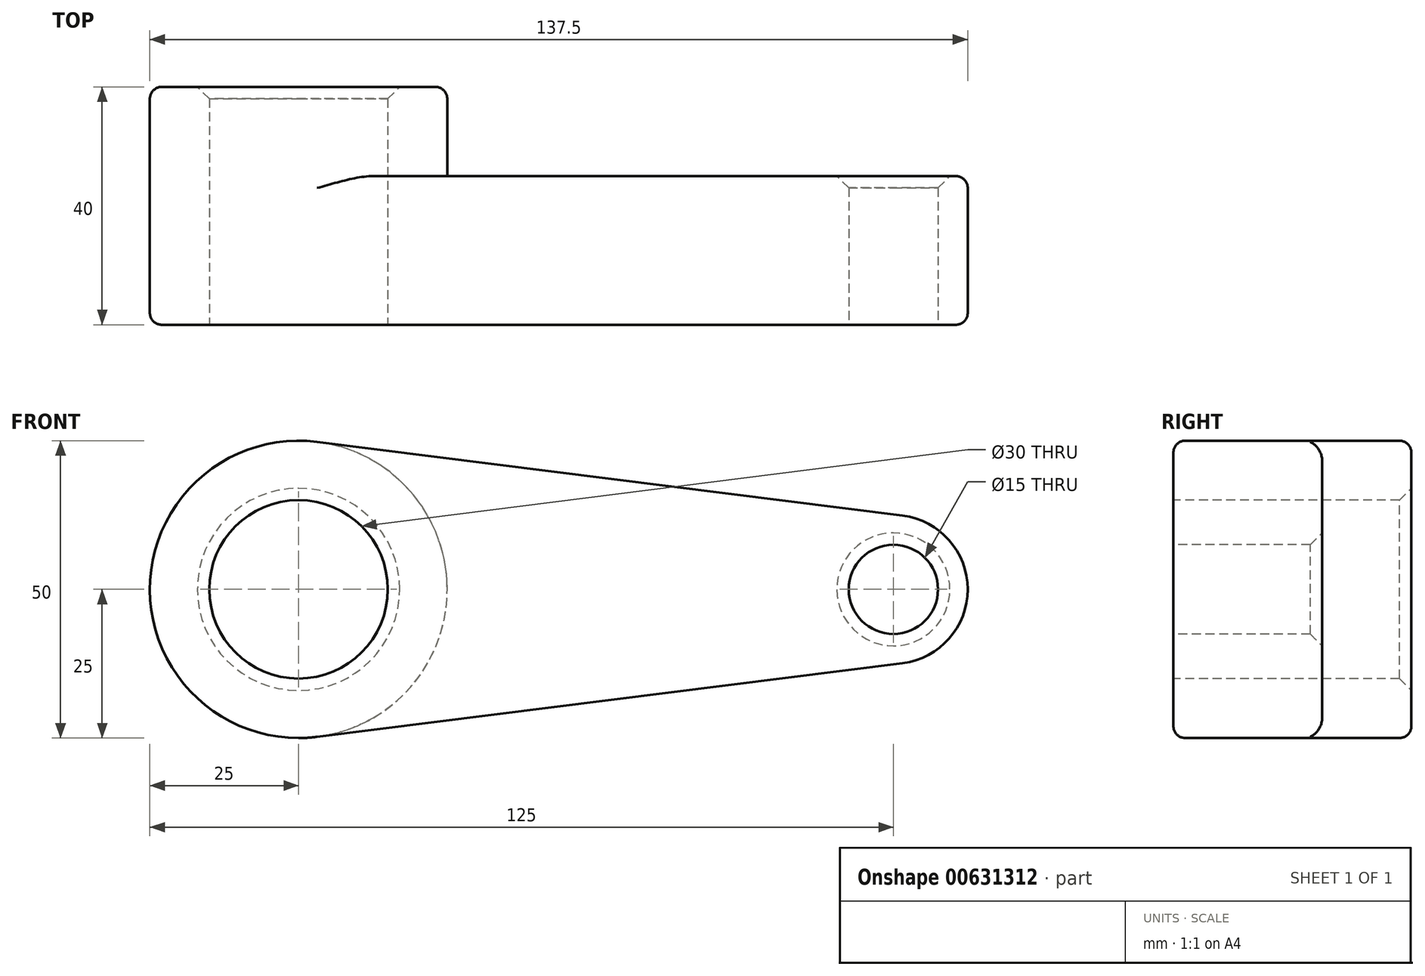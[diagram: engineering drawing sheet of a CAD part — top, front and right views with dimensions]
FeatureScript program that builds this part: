
annotation { "Feature Type Name" : "Feature", "Feature Type Description" : "" }
export const myFeature = defineFeature(function(context is Context, id is Id, definition is map)
    precondition{}
    {
        {
            var Q0;
            Q0=qCreatedBy(makeId("Front.planeOp"),FACE);
            var sketch = newSketch(context, id + "F0", { "sketchPlane" : qUnion([Q0])});
            skCircle(sketch, "E0", {"center": v(0, 0) * mm, "radius": 25 * mm});
            skCircle(sketch, "E1", {"center": v(100, 0) * mm, "radius": 12.5 * mm});
            skLineSegment(sketch, "E2", {"start": v(3.12, 24.8) * mm, "end": v(101.56, 12.4) * mm});
            skLineSegment(sketch, "E3", {"start": v(3.13, -24.8) * mm, "end": v(101.56, -12.4) * mm});
            skCircle(sketch, "E4", {"center": v(0, 0) * mm, "radius": 15 * mm});
            skCircle(sketch, "E5", {"center": v(100, 0) * mm, "radius": 7.5 * mm});
            skSolve(sketch);
        }
        {
            var Q0;
            Q0 = qSketchRegion(id + "F0", true);
            extrude(context, id + "F1", {"entities" : qUnion([Q0]), "oppositeDirection" : true, "depth" : 25 * mm, "offsetDistance" : 25 * mm});
        }
        {
            var Q0;
            Q0=makeQuery(id+"F0.imprint","IMPRINT",FACE,{"disambiguationData":[TD([[makeQuery(id+"F0.imprint","IMPRINT",EDGE,{"derivedFrom":sQuery(id+"F0.wireOp",EDGE,"E4")}),-1.0]])]});
            extrude(context, id + "F2", {"entities" : qUnion([Q0]), "operationType" : NewBodyOperationType.ADD, "oppositeDirection" : true, "depth" : 40 * mm, "offsetDistance" : 25 * mm});
        }
        {
            var Q0;
            Q0=makeQuery(id+"F1.opExtrude","CAP_EDGE",EDGE,{"disambiguationData":[OSD([sQuery(id+"F0.wireOp",EDGE,"E2")])],"isStart":false});
            var Q1;
            Q1=makeQuery(id+"F1.opExtrude","CAP_EDGE",EDGE,{"disambiguationData":[OSD([sQuery(id+"F0.wireOp",EDGE,"E2")])],"isStart":true});
            var Q2;
            Q2=makeQuery(id+"F2.opExtrude","CAP_EDGE",EDGE,{"disambiguationData":[OSD([sQuery(id+"F0.wireOp",EDGE,"E0")])],"isStart":false});
            fillet(context, id + "F3", {"entities" : qUnion([Q0, Q1, Q2]), "radius" : 2 * mm, "tangentPropagation" : true, "allowEdgeOverflow" : false});
        }
        {
            var Q0;
            Q0=makeQuery(id+"F2.opExtrude","CAP_EDGE",EDGE,{"disambiguationData":[OSD([sQuery(id+"F0.wireOp",EDGE,"E4")])],"isStart":false});
            var Q1;
            Q1=makeQuery(id+"F1.opExtrude","CAP_EDGE",EDGE,{"disambiguationData":[OSD([sQuery(id+"F0.wireOp",EDGE,"E5")])],"isStart":false});
            chamfer(context, id + "F4", {"entities" : qUnion([Q0, Q1]), "width" : 2 * mm, "tangentPropagation" : true});
        }
    });
